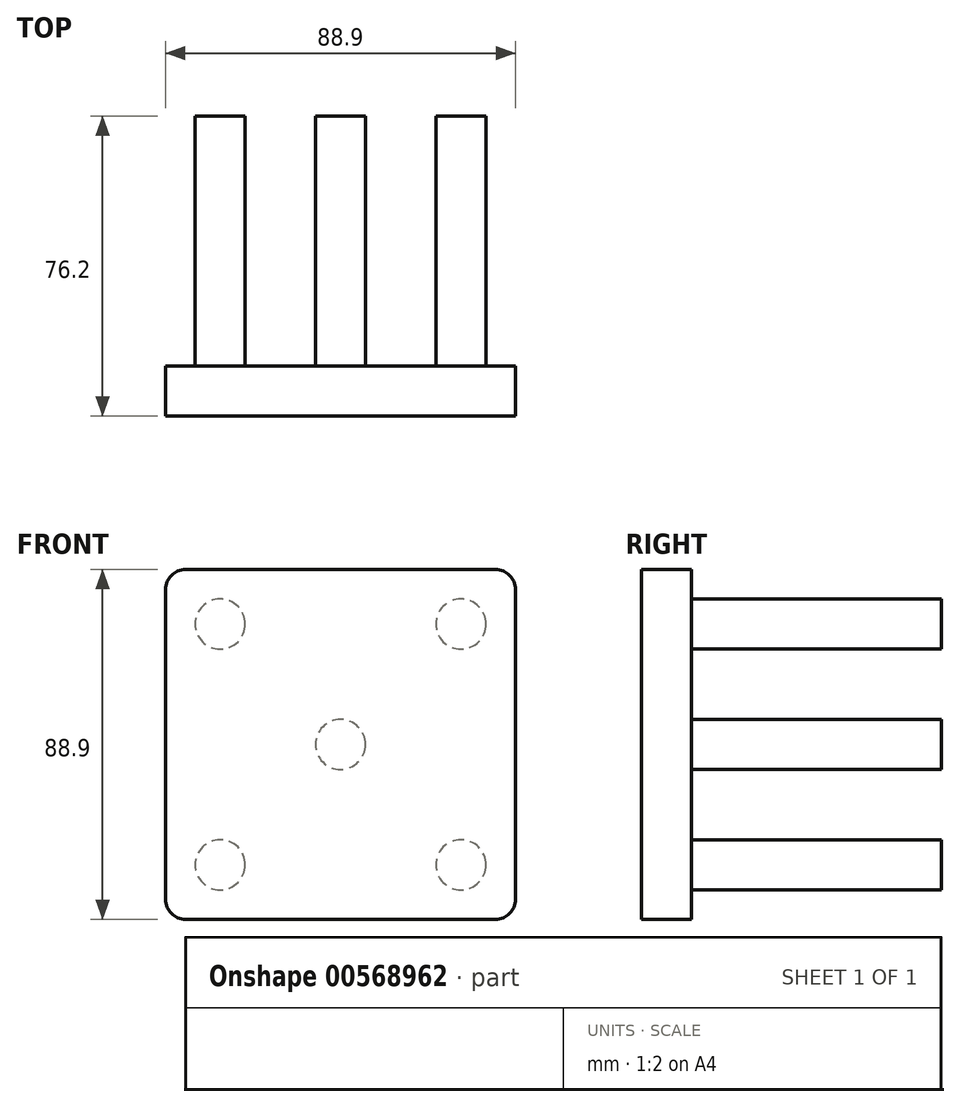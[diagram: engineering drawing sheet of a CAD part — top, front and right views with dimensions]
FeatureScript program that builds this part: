
annotation { "Feature Type Name" : "Feature", "Feature Type Description" : "" }
export const myFeature = defineFeature(function(context is Context, id is Id, definition is map)
    precondition{}
    {
        {
            var Q0;
            Q0=qCreatedBy(makeId("Front.planeOp"),FACE);
            var sketch = newSketch(context, id + "F0", { "sketchPlane" : qUnion([Q0])});
            skLineSegment(sketch, "E0.bottom", {"start": v(-54.17, 33.71) * mm, "end": v(34.73, 33.71) * mm});
            skLineSegment(sketch, "E0.top", {"start": v(-54.17, -55.19) * mm, "end": v(34.73, -55.19) * mm});
            skLineSegment(sketch, "E0.left", {"start": v(-54.17, 33.71) * mm, "end": v(-54.17, -55.19) * mm});
            skLineSegment(sketch, "E0.right", {"start": v(34.73, 33.71) * mm, "end": v(34.73, -55.19) * mm});
            skCircle(sketch, "E1", {"center": v(-9.72, -10.74) * mm, "radius": 6.35 * mm});
            skCircle(sketch, "E2", {"center": v(-40.3, 19.85) * mm, "radius": 6.35 * mm});
            skCircle(sketch, "E3", {"center": v(20.86, 19.85) * mm, "radius": 6.35 * mm});
            skCircle(sketch, "E4", {"center": v(-40.3, -41.32) * mm, "radius": 6.35 * mm});
            skCircle(sketch, "E5", {"center": v(20.86, -41.32) * mm, "radius": 6.35 * mm});
            skLineSegment(sketch, "E6", {"start": v(-9.72, 33.71) * mm, "end": v(-9.72, -55.19) * mm, "construction": true});
            skLineSegment(sketch, "E7", {"start": v(-54.17, -10.74) * mm, "end": v(34.73, -10.74) * mm, "construction": true});
            skLineSegment(sketch, "E8", {"start": v(-54.17, 33.71) * mm, "end": v(34.73, -55.19) * mm, "construction": true});
            skLineSegment(sketch, "E9", {"start": v(-54.17, -55.19) * mm, "end": v(34.73, 33.71) * mm, "construction": true});
            skSolve(sketch);
        }
        {
            var Q0;
            Q0=makeQuery(id+"F0.imprint","IMPRINT",FACE,{"disambiguationData":[TD([[makeQuery(id+"F0.imprint","IMPRINT",EDGE,{"derivedFrom":sQuery(id+"F0.wireOp",EDGE,"E0.bottom")}),-1.0]])]});
            extrude(context, id + "F1", {"entities" : qUnion([Q0]), "oppositeDirection" : true, "depth" : 12.7 * mm, "offsetDistance" : 25.4 * mm});
        }
        {
            var Q0;
            Q0=makeQuery(id+"F0.imprint","IMPRINT",FACE,{"disambiguationData":[TD([[makeQuery(id+"F0.imprint","IMPRINT",EDGE,{"derivedFrom":sQuery(id+"F0.wireOp",EDGE,"E2")}),1.0]])]});
            var Q1;
            Q1=makeQuery(id+"F0.imprint","IMPRINT",FACE,{"disambiguationData":[TD([[makeQuery(id+"F0.imprint","IMPRINT",EDGE,{"derivedFrom":sQuery(id+"F0.wireOp",EDGE,"E3")}),1.0]])]});
            var Q2;
            Q2=makeQuery(id+"F0.imprint","IMPRINT",FACE,{"disambiguationData":[TD([[makeQuery(id+"F0.imprint","IMPRINT",EDGE,{"derivedFrom":sQuery(id+"F0.wireOp",EDGE,"E1")}),1.0]])]});
            var Q3;
            Q3=makeQuery(id+"F0.imprint","IMPRINT",FACE,{"disambiguationData":[TD([[makeQuery(id+"F0.imprint","IMPRINT",EDGE,{"derivedFrom":sQuery(id+"F0.wireOp",EDGE,"E5")}),1.0]])]});
            var Q4;
            Q4=makeQuery(id+"F0.imprint","IMPRINT",FACE,{"disambiguationData":[TD([[makeQuery(id+"F0.imprint","IMPRINT",EDGE,{"derivedFrom":sQuery(id+"F0.wireOp",EDGE,"E4")}),1.0]])]});
            extrude(context, id + "F2", {"entities" : qUnion([Q0, Q1, Q2, Q3, Q4]), "operationType" : NewBodyOperationType.ADD, "oppositeDirection" : true, "depth" : 76.2 * mm, "offsetDistance" : 25.4 * mm});
        }
        {
            var Q0;
            Q0=makeQuery(id+"F1.opExtrude","SWEPT_EDGE",EDGE,{"disambiguationData":[OSD([sQuery(id+"F0.wireOp",EDGE,"E0.bottom"),sQuery(id+"F0.wireOp",EDGE,"E0.right")])]});
            var Q1;
            Q1=makeQuery(id+"F1.opExtrude","SWEPT_EDGE",EDGE,{"disambiguationData":[OSD([sQuery(id+"F0.wireOp",EDGE,"E0.bottom"),sQuery(id+"F0.wireOp",EDGE,"E0.left")])]});
            var Q2;
            Q2=makeQuery(id+"F1.opExtrude","SWEPT_EDGE",EDGE,{"disambiguationData":[OSD([sQuery(id+"F0.wireOp",EDGE,"E0.top"),sQuery(id+"F0.wireOp",EDGE,"E0.left")])]});
            var Q3;
            Q3=makeQuery(id+"F1.opExtrude","SWEPT_EDGE",EDGE,{"disambiguationData":[OSD([sQuery(id+"F0.wireOp",EDGE,"E0.top"),sQuery(id+"F0.wireOp",EDGE,"E0.right")])]});
            var Q4;
            Q4=makeQuery(id+"F1.opExtrude","CAP_EDGE",EDGE,{"disambiguationData":[OSD([sQuery(id+"F0.wireOp",EDGE,"E3")])],"isStart":false});
            var Q5;
            Q5=makeQuery(id+"F1.opExtrude","CAP_EDGE",EDGE,{"disambiguationData":[OSD([sQuery(id+"F0.wireOp",EDGE,"E2")])],"isStart":false});
            var Q6;
            Q6=makeQuery(id+"F1.opExtrude","CAP_EDGE",EDGE,{"disambiguationData":[OSD([sQuery(id+"F0.wireOp",EDGE,"E1")])],"isStart":false});
            var Q7;
            Q7=makeQuery(id+"F1.opExtrude","CAP_EDGE",EDGE,{"disambiguationData":[OSD([sQuery(id+"F0.wireOp",EDGE,"E4")])],"isStart":false});
            var Q8;
            Q8=makeQuery(id+"F1.opExtrude","CAP_EDGE",EDGE,{"disambiguationData":[OSD([sQuery(id+"F0.wireOp",EDGE,"E5")])],"isStart":false});
            fillet(context, id + "F3", {"entities" : qUnion([Q0, Q1, Q2, Q3, Q4, Q5, Q6, Q7, Q8]), "radius" : 5.08 * mm, "tangentPropagation" : true, "allowEdgeOverflow" : false});
        }
    });
